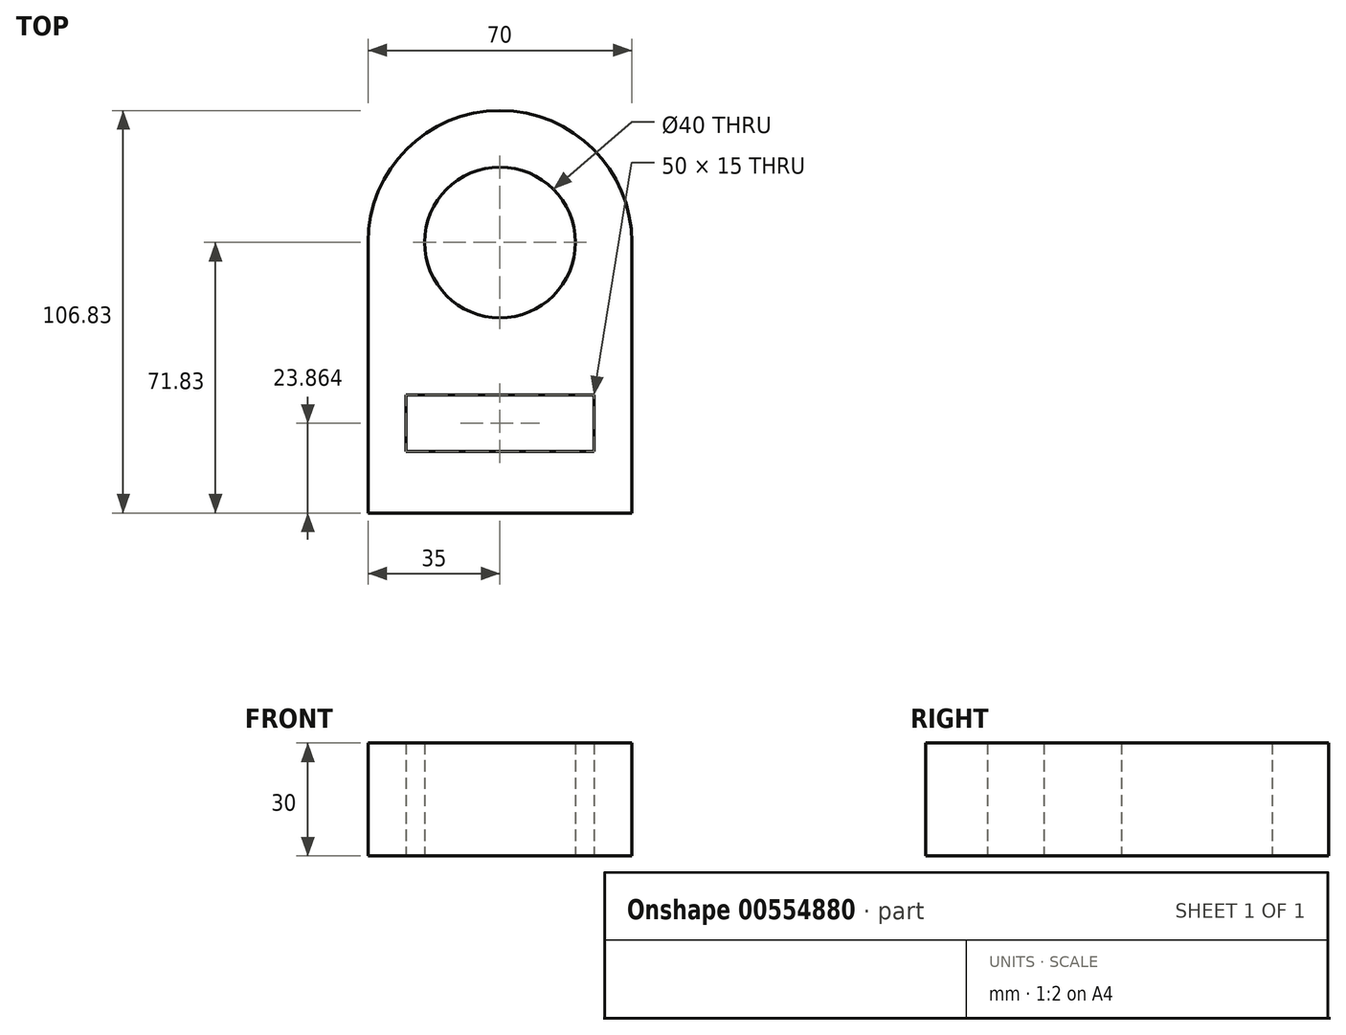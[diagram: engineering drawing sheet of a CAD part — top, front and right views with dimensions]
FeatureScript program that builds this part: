
annotation { "Feature Type Name" : "Feature", "Feature Type Description" : "" }
export const myFeature = defineFeature(function(context is Context, id is Id, definition is map)
    precondition{}
    {
        {
            var Q0;
            Q0=qCreatedBy(makeId("Top.planeOp"),FACE);
            var sketch = newSketch(context, id + "F0", { "sketchPlane" : qUnion([Q0])});
            skCircle(sketch, "E0", {"center": v(0, 0) * mm, "radius": 20 * mm});
            skArc(sketch, "E1", {"start": v(35, 0) * mm, "mid": v(0, 35) * mm, "end": v(-35, 0) * mm});
            skLineSegment(sketch, "E2", {"start": v(-35, -71.83) * mm, "end": v(35, -71.83) * mm});
            skLineSegment(sketch, "E3", {"start": v(35, 0) * mm, "end": v(35, -71.83) * mm});
            skLineSegment(sketch, "E4", {"start": v(-35, 0) * mm, "end": v(-35, -71.83) * mm});
            skLineSegment(sketch, "E5", {"start": v(0, -40.47) * mm, "end": v(-25, -40.47) * mm});
            skLineSegment(sketch, "E6", {"start": v(0, -40.47) * mm, "end": v(25, -40.47) * mm});
            skLineSegment(sketch, "E7", {"start": v(-25, -40.47) * mm, "end": v(-25, -55.47) * mm});
            skLineSegment(sketch, "E8", {"start": v(25, -40.47) * mm, "end": v(25, -55.47) * mm});
            skLineSegment(sketch, "E9", {"start": v(-25, -55.47) * mm, "end": v(25, -55.47) * mm});
            skSolve(sketch);
        }
        {
            var Q0;
            Q0 = qSketchRegion(id + "F0", true);
            extrude(context, id + "F1", {"entities" : qUnion([Q0]), "depth" : 30 * mm, "offsetDistance" : 25 * mm});
        }
    });
